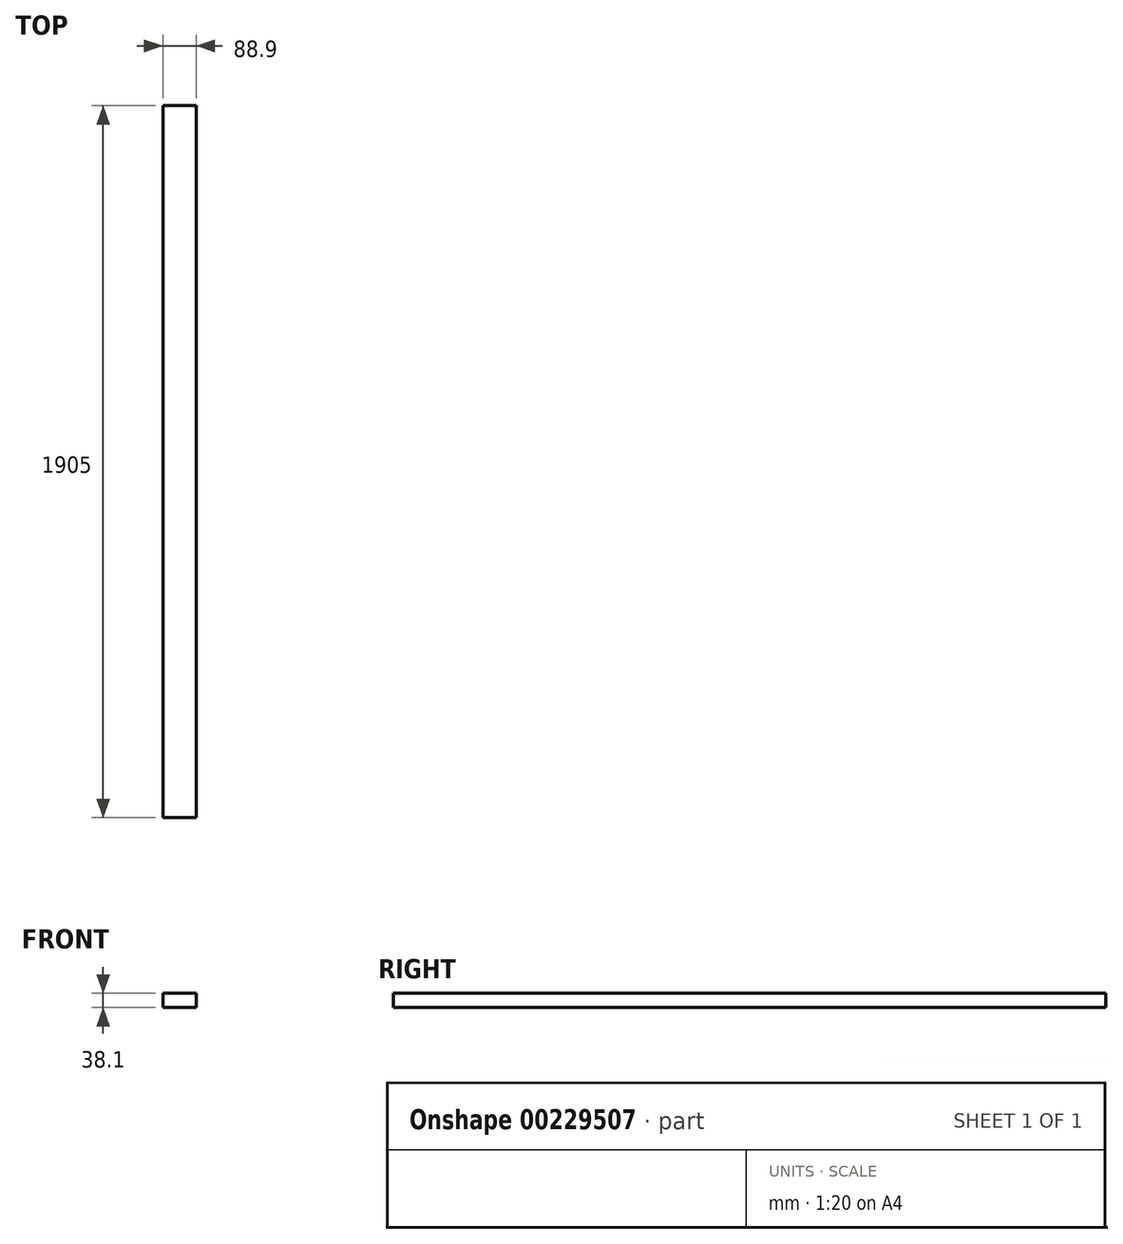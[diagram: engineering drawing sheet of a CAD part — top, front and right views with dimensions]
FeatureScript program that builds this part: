
annotation { "Feature Type Name" : "Feature", "Feature Type Description" : "" }
export const myFeature = defineFeature(function(context is Context, id is Id, definition is map)
    precondition{}
    {
        {
            var Q0;
            Q0=qCreatedBy(makeId("Front.planeOp"),FACE);
            var sketch = newSketch(context, id + "F0", { "sketchPlane" : qUnion([Q0])});
            skLineSegment(sketch, "E0.bottom", {"start": v(0, 0) * mm, "end": v(88.9, 0) * mm});
            skLineSegment(sketch, "E0.top", {"start": v(0, -38.1) * mm, "end": v(88.9, -38.1) * mm});
            skLineSegment(sketch, "E0.left", {"start": v(0, 0) * mm, "end": v(0, -38.1) * mm});
            skLineSegment(sketch, "E0.right", {"start": v(88.9, 0) * mm, "end": v(88.9, -38.1) * mm});
            skSolve(sketch);
        }
        {
            var Q0;
            Q0=qSketchRegion(id+"F0",true);
            extrude(context, id + "F1", {"entities" : qUnion([Q0]), "depth" : 1905 * mm});
        }
    });
